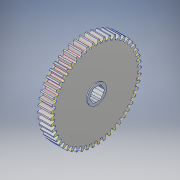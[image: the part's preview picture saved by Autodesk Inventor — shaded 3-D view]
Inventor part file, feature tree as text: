
AUTODESK INVENTOR PART (.ipt)
format: ipt  version: 2018 (Build 220112000, 112)  size: 442,368 bytes
history: native  units: in
note: dims shown in document units (in); Inventor stores cm internally (conversion verified against a paired STEP export)
features: other x3, sketch x1
ambient origin geometry x8: Origin, YZ Plane, XZ Plane, XY Plane, X Axis, Y Axis, Z Axis, Center Point
bodies: Solid1 (feature_tree)
feature tree (4):
  sketch  "Sketch1"  dims[d0=2.5in d1=1.0in d2=0.0in]
  other  "Srf1"
  other  "Cut-Extrude2"
  other  "PITCH CIRCLE"
